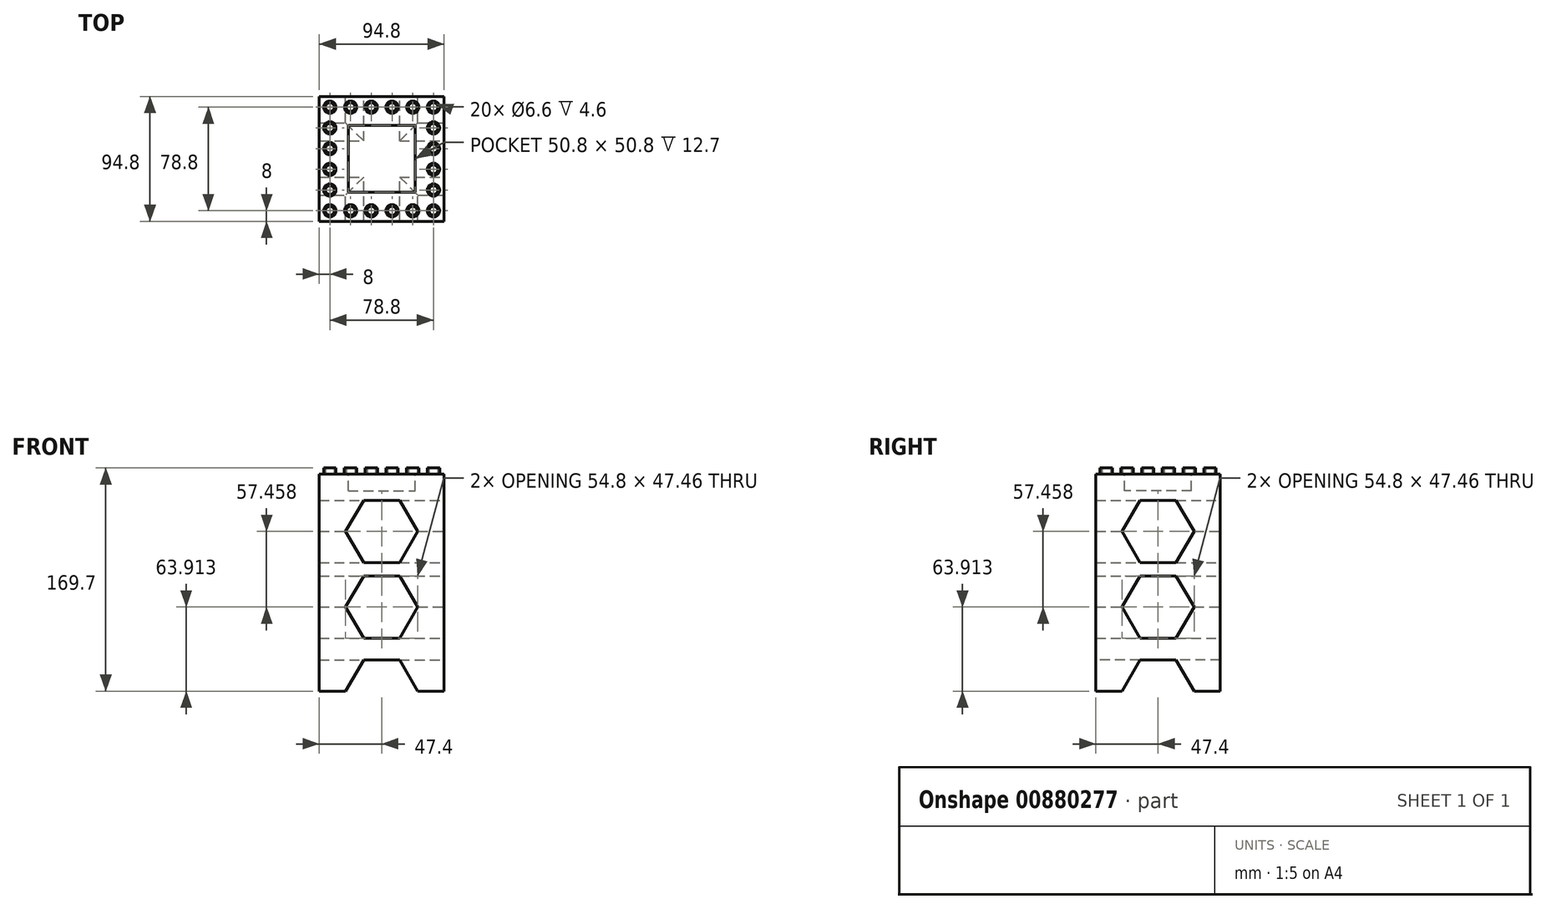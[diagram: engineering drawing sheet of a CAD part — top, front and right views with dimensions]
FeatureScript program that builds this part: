
annotation { "Feature Type Name" : "Feature", "Feature Type Description" : "" }
export const myFeature = defineFeature(function(context is Context, id is Id, definition is map)
    precondition{}
    {
        {
            var Q0;
            Q0=qCreatedBy(makeId("Top.planeOp"),FACE);
            var sketch = newSketch(context, id + "F0", { "sketchPlane" : qUnion([Q0])});
            skLineSegment(sketch, "E0.bottom", {"start": v(-25.4, 25.4) * mm, "end": v(25.4, 25.4) * mm});
            skLineSegment(sketch, "E0.top", {"start": v(-25.4, -25.4) * mm, "end": v(25.4, -25.4) * mm});
            skLineSegment(sketch, "E0.left", {"start": v(-25.4, 25.4) * mm, "end": v(-25.4, -25.4) * mm});
            skLineSegment(sketch, "E0.right", {"start": v(25.4, 25.4) * mm, "end": v(25.4, -25.4) * mm});
            skLineSegment(sketch, "E1.bottom", {"start": v(-47.4, 47.4) * mm, "end": v(47.4, 47.4) * mm});
            skLineSegment(sketch, "E1.top", {"start": v(-47.4, -47.4) * mm, "end": v(47.4, -47.4) * mm});
            skLineSegment(sketch, "E1.left", {"start": v(-47.4, 47.4) * mm, "end": v(-47.4, -47.4) * mm});
            skLineSegment(sketch, "E1.right", {"start": v(47.4, 47.4) * mm, "end": v(47.4, -47.4) * mm});
            skLineSegment(sketch, "E2", {"start": v(0, 25.4) * mm, "end": v(0, -25.4) * mm, "construction": true});
            skSolve(sketch);
        }
        {
            var Q0;
            Q0=makeQuery(id+"F0.imprint","IMPRINT",FACE,{"disambiguationData":[TD([[makeQuery(id+"F0.imprint","IMPRINT",EDGE,{"derivedFrom":sQuery(id+"F0.wireOp",EDGE,"E0.bottom")}),1.0]])]});
            var Q1;
            Q1=makeQuery(id+"F0.imprint","IMPRINT",FACE,{"disambiguationData":[TD([[makeQuery(id+"F0.imprint","IMPRINT",EDGE,{"derivedFrom":sQuery(id+"F0.wireOp",EDGE,"E0.bottom")}),-1.0]])]});
            extrude(context, id + "F1", {"entities" : qUnion([Q0, Q1]), "oppositeDirection" : true, "depth" : 165.1 * mm, "offsetDistance" : 25 * mm});
        }
        {
            var Q0;
            Q0=makeQuery(id+"F0.imprint","IMPRINT",FACE,{"disambiguationData":[TD([[makeQuery(id+"F0.imprint","IMPRINT",EDGE,{"derivedFrom":sQuery(id+"F0.wireOp",EDGE,"E0.bottom")}),-1.0]])]});
            extrude(context, id + "F2", {"entities" : qUnion([Q0]), "operationType" : NewBodyOperationType.REMOVE, "flatOperationType" : FlatOperationType.REMOVE, "oppositeDirection" : true, "depth" : 12.7 * mm, "offsetDistance" : 25 * mm, "domain" : OperationDomain.MODEL});
        }
        {
            var Q0;
            Q0=makeQuery(id+"F1.opExtrude","SWEPT_FACE",FACE,{"disambiguationData":[OSD([sQuery(id+"F0.wireOp",EDGE,"E1.right")])]});
            var sketch = newSketch(context, id + "F3", { "sketchPlane" : qUnion([Q0])});
            skLineSegment(sketch, "E3", {"start": v(0, -165.1) * mm, "end": v(0, -127.29) * mm});
            skCircle(sketch, "E4.cCircle", {"center": v(0, -165.1) * mm, "radius": 23.73 * mm, "construction": true});
            skLineSegment(sketch, "E4.0", {"start": v(-13.7, -141.37) * mm, "end": v(13.7, -141.37) * mm});
            skLineSegment(sketch, "E4.1", {"start": v(13.7, -141.37) * mm, "end": v(27.4, -165.1) * mm});
            skLineSegment(sketch, "E4.2", {"start": v(27.4, -165.1) * mm, "end": v(13.7, -188.83) * mm});
            skLineSegment(sketch, "E4.3", {"start": v(13.7, -188.83) * mm, "end": v(-13.7, -188.83) * mm});
            skLineSegment(sketch, "E4.4", {"start": v(-13.7, -188.83) * mm, "end": v(-27.4, -165.1) * mm});
            skLineSegment(sketch, "E4.5", {"start": v(-27.4, -165.1) * mm, "end": v(-13.7, -141.37) * mm});
            skPoint(sketch, "E4.0.midPoint", {"position": v(0, -141.37) * mm});
            skSolve(sketch);
        }
        {
            var Q0;
            Q0 = qSketchRegion(id + "F3", true);
            extrude(context, id + "F4", {"entities" : qUnion([Q0]), "operationType" : NewBodyOperationType.REMOVE, "oppositeDirection" : true, "depth" : 101.3 * mm, "offsetDistance" : 25 * mm});
        }
        {
            var Q0;
            Q0=makeQuery(id+"F1.opExtrude","SWEPT_FACE",FACE,{"disambiguationData":[OSD([sQuery(id+"F0.wireOp",EDGE,"E1.top")])]});
            var sketch = newSketch(context, id + "F5", { "sketchPlane" : qUnion([Q0])});
            skCircle(sketch, "E5.cCircle", {"center": v(0, -165.1) * mm, "radius": 23.73 * mm, "construction": true});
            skLineSegment(sketch, "E5.0", {"start": v(-13.7, -141.37) * mm, "end": v(13.7, -141.37) * mm});
            skLineSegment(sketch, "E5.1", {"start": v(13.7, -141.37) * mm, "end": v(27.4, -165.1) * mm});
            skLineSegment(sketch, "E5.2", {"start": v(27.4, -165.1) * mm, "end": v(13.7, -188.83) * mm});
            skLineSegment(sketch, "E5.3", {"start": v(13.7, -188.83) * mm, "end": v(-13.7, -188.83) * mm});
            skLineSegment(sketch, "E5.4", {"start": v(-13.7, -188.83) * mm, "end": v(-27.4, -165.1) * mm});
            skLineSegment(sketch, "E5.5", {"start": v(-27.4, -165.1) * mm, "end": v(-13.7, -141.37) * mm});
            skPoint(sketch, "E5.0.midPoint", {"position": v(0, -141.37) * mm});
            skSolve(sketch);
        }
        {
            var Q0;
            Q0=makeQuery(id+"F5.imprint","IMPRINT",FACE,{"disambiguationData":[TD([[makeQuery(id+"F5.imprint","IMPRINT",EDGE,{"derivedFrom":sQuery(id+"F5.wireOp",EDGE,"E5.0")}),-1.0]])]});
            extrude(context, id + "F6", {"entities" : qUnion([Q0]), "operationType" : NewBodyOperationType.REMOVE, "oppositeDirection" : true, "depth" : 114 * mm, "offsetDistance" : 25 * mm});
        }
        {
            var Q0;
            Q0=makeQuery(id+"F1.opExtrude","SWEPT_FACE",FACE,{"disambiguationData":[OSD([sQuery(id+"F0.wireOp",EDGE,"E1.bottom")])]});
            var sketch = newSketch(context, id + "F7", { "sketchPlane" : qUnion([Q0])});
            skCircle(sketch, "E6.cCircle", {"center": v(0, -43.73) * mm, "radius": 23.73 * mm, "construction": true});
            skLineSegment(sketch, "E6.0", {"start": v(-13.7, -20) * mm, "end": v(13.7, -20) * mm});
            skLineSegment(sketch, "E6.1", {"start": v(13.7, -20) * mm, "end": v(27.4, -43.73) * mm});
            skLineSegment(sketch, "E6.2", {"start": v(27.4, -43.73) * mm, "end": v(13.7, -67.46) * mm});
            skLineSegment(sketch, "E6.3", {"start": v(13.7, -67.46) * mm, "end": v(-13.7, -67.46) * mm});
            skLineSegment(sketch, "E6.4", {"start": v(-13.7, -67.46) * mm, "end": v(-27.4, -43.73) * mm});
            skLineSegment(sketch, "E6.5", {"start": v(-27.4, -43.73) * mm, "end": v(-13.7, -20) * mm});
            skPoint(sketch, "E6.0.midPoint", {"position": v(0, -20) * mm});
            skCircle(sketch, "E7.cCircle", {"center": v(0, -101.19) * mm, "radius": 23.73 * mm, "construction": true});
            skLineSegment(sketch, "E7.0", {"start": v(-13.7, -77.46) * mm, "end": v(13.7, -77.46) * mm});
            skLineSegment(sketch, "E7.1", {"start": v(13.7, -77.46) * mm, "end": v(27.4, -101.19) * mm});
            skLineSegment(sketch, "E7.2", {"start": v(27.4, -101.19) * mm, "end": v(13.7, -124.92) * mm});
            skLineSegment(sketch, "E7.3", {"start": v(13.7, -124.92) * mm, "end": v(-13.7, -124.92) * mm});
            skLineSegment(sketch, "E7.4", {"start": v(-13.7, -124.92) * mm, "end": v(-27.4, -101.19) * mm});
            skLineSegment(sketch, "E7.5", {"start": v(-27.4, -101.19) * mm, "end": v(-13.7, -77.46) * mm});
            skPoint(sketch, "E7.0.midPoint", {"position": v(0, -77.46) * mm});
            skLineSegment(sketch, "E8", {"start": v(60.92, 0) * mm, "end": v(60.92, -12.7) * mm});
            skSolve(sketch);
        }
        {
            var Q0;
            Q0=makeQuery(id+"F7.imprint","IMPRINT",FACE,{"disambiguationData":[TD([[makeQuery(id+"F7.imprint","IMPRINT",EDGE,{"derivedFrom":sQuery(id+"F7.wireOp",EDGE,"E6.0")}),-1.0]])]});
            extrude(context, id + "F8", {"entities" : qUnion([Q0]), "operationType" : NewBodyOperationType.REMOVE, "oppositeDirection" : true, "depth" : 110 * mm, "offsetDistance" : 25 * mm});
        }
        {
            var Q0;
            Q0=makeQuery(id+"F7.imprint","IMPRINT",FACE,{"disambiguationData":[TD([[makeQuery(id+"F7.imprint","IMPRINT",EDGE,{"derivedFrom":sQuery(id+"F7.wireOp",EDGE,"E7.0")}),-1.0]])]});
            extrude(context, id + "F9", {"entities" : qUnion([Q0]), "operationType" : NewBodyOperationType.REMOVE, "oppositeDirection" : true, "depth" : 114 * mm, "offsetDistance" : 25 * mm});
        }
        {
            var Q0;
            Q0=makeQuery(id+"F1.opExtrude","SWEPT_FACE",FACE,{"disambiguationData":[OSD([sQuery(id+"F0.wireOp",EDGE,"E1.right")])]});
            var sketch = newSketch(context, id + "F10", { "sketchPlane" : qUnion([Q0])});
            skCircle(sketch, "E9.cCircle", {"center": v(0, -43.73) * mm, "radius": 23.73 * mm, "construction": true});
            skLineSegment(sketch, "E9.0", {"start": v(-13.7, -20) * mm, "end": v(13.7, -20) * mm});
            skLineSegment(sketch, "E9.1", {"start": v(13.7, -20) * mm, "end": v(27.4, -43.73) * mm});
            skLineSegment(sketch, "E9.2", {"start": v(27.4, -43.73) * mm, "end": v(13.7, -67.46) * mm});
            skLineSegment(sketch, "E9.3", {"start": v(13.7, -67.46) * mm, "end": v(-13.7, -67.46) * mm});
            skLineSegment(sketch, "E9.4", {"start": v(-13.7, -67.46) * mm, "end": v(-27.4, -43.73) * mm});
            skLineSegment(sketch, "E9.5", {"start": v(-27.4, -43.73) * mm, "end": v(-13.7, -20) * mm});
            skPoint(sketch, "E9.0.midPoint", {"position": v(0, -20) * mm});
            skCircle(sketch, "E10.cCircle", {"center": v(0, -101.19) * mm, "radius": 23.73 * mm, "construction": true});
            skLineSegment(sketch, "E10.0", {"start": v(-13.7, -77.46) * mm, "end": v(13.7, -77.46) * mm});
            skLineSegment(sketch, "E10.1", {"start": v(13.7, -77.46) * mm, "end": v(27.4, -101.19) * mm});
            skLineSegment(sketch, "E10.2", {"start": v(27.4, -101.19) * mm, "end": v(13.7, -124.92) * mm});
            skLineSegment(sketch, "E10.3", {"start": v(13.7, -124.92) * mm, "end": v(-13.7, -124.92) * mm});
            skLineSegment(sketch, "E10.4", {"start": v(-13.7, -124.92) * mm, "end": v(-27.4, -101.19) * mm});
            skLineSegment(sketch, "E10.5", {"start": v(-27.4, -101.19) * mm, "end": v(-13.7, -77.46) * mm});
            skPoint(sketch, "E10.0.midPoint", {"position": v(0, -77.46) * mm});
            skSolve(sketch);
        }
        {
            var Q0;
            Q0=makeQuery(id+"F10.imprint","IMPRINT",FACE,{"disambiguationData":[TD([[makeQuery(id+"F10.imprint","IMPRINT",EDGE,{"derivedFrom":sQuery(id+"F10.wireOp",EDGE,"E9.0")}),-1.0]])]});
            var Q1;
            Q1=makeQuery(id+"F10.imprint","IMPRINT",FACE,{"disambiguationData":[TD([[makeQuery(id+"F10.imprint","IMPRINT",EDGE,{"derivedFrom":sQuery(id+"F10.wireOp",EDGE,"E10.0")}),-1.0]])]});
            extrude(context, id + "F11", {"entities" : qUnion([Q0, Q1]), "operationType" : NewBodyOperationType.REMOVE, "oppositeDirection" : true, "depth" : 115 * mm, "offsetDistance" : 25 * mm});
        }
        {
            var Q0;
            Q0=makeQuery(id+"F0.imprint","IMPRINT",FACE,{"disambiguationData":[TD([[makeQuery(id+"F0.imprint","IMPRINT",EDGE,{"derivedFrom":sQuery(id+"F0.wireOp",EDGE,"E0.bottom")}),1.0]])]});
            var sketch = newSketch(context, id + "F12", { "sketchPlane" : qUnion([Q0])});
            skCircle(sketch, "E11", {"center": v(39.4, 39.4) * mm, "radius": 4.7 * mm});
            skCircle(sketch, "E12.0.1.0", {"center": v(39.4, 23.64) * mm, "radius": 4.7 * mm});
            skCircle(sketch, "E12.0.2.0", {"center": v(39.4, 7.88) * mm, "radius": 4.7 * mm});
            skCircle(sketch, "E12.0.3.0", {"center": v(39.4, -7.88) * mm, "radius": 4.7 * mm});
            skCircle(sketch, "E12.0.4.0", {"center": v(39.4, -23.64) * mm, "radius": 4.7 * mm});
            skCircle(sketch, "E12.0.5.0", {"center": v(39.4, -39.4) * mm, "radius": 4.7 * mm});
            skCircle(sketch, "E12.1.0.0", {"center": v(23.64, 39.4) * mm, "radius": 4.7 * mm});
            skCircle(sketch, "E12.1.5.0", {"center": v(23.64, -39.4) * mm, "radius": 4.7 * mm});
            skCircle(sketch, "E12.2.0.0", {"center": v(7.88, 39.4) * mm, "radius": 4.7 * mm});
            skCircle(sketch, "E12.2.5.0", {"center": v(7.88, -39.4) * mm, "radius": 4.7 * mm});
            skCircle(sketch, "E12.3.0.0", {"center": v(-7.88, 39.4) * mm, "radius": 4.7 * mm});
            skCircle(sketch, "E12.3.5.0", {"center": v(-7.88, -39.4) * mm, "radius": 4.7 * mm});
            skCircle(sketch, "E12.4.0.0", {"center": v(-23.64, 39.4) * mm, "radius": 4.7 * mm});
            skCircle(sketch, "E12.4.5.0", {"center": v(-23.64, -39.4) * mm, "radius": 4.7 * mm});
            skCircle(sketch, "E12.5.0.0", {"center": v(-39.4, 39.4) * mm, "radius": 4.7 * mm});
            skCircle(sketch, "E12.5.1.0", {"center": v(-39.4, 23.64) * mm, "radius": 4.7 * mm});
            skCircle(sketch, "E12.5.2.0", {"center": v(-39.4, 7.88) * mm, "radius": 4.7 * mm});
            skCircle(sketch, "E12.5.3.0", {"center": v(-39.4, -7.88) * mm, "radius": 4.7 * mm});
            skCircle(sketch, "E12.5.4.0", {"center": v(-39.4, -23.64) * mm, "radius": 4.7 * mm});
            skCircle(sketch, "E12.5.5.0", {"center": v(-39.4, -39.4) * mm, "radius": 4.7 * mm});
            skLineSegment(sketch, "E12.direction1", {"start": v(39.4, 39.4) * mm, "end": v(23.64, 39.4) * mm, "construction": true});
            skLineSegment(sketch, "E12.direction2", {"start": v(39.4, 39.4) * mm, "end": v(39.4, 23.64) * mm, "construction": true});
            skCircle(sketch, "E13", {"center": v(39.4, 39.4) * mm, "radius": 3.3 * mm});
            skCircle(sketch, "E14.0.1.0", {"center": v(39.4, 23.64) * mm, "radius": 3.3 * mm});
            skCircle(sketch, "E14.0.2.0", {"center": v(39.4, 7.88) * mm, "radius": 3.3 * mm});
            skCircle(sketch, "E14.0.3.0", {"center": v(39.4, -7.88) * mm, "radius": 3.3 * mm});
            skCircle(sketch, "E14.0.4.0", {"center": v(39.4, -23.64) * mm, "radius": 3.3 * mm});
            skCircle(sketch, "E14.0.5.0", {"center": v(39.4, -39.4) * mm, "radius": 3.3 * mm});
            skCircle(sketch, "E14.1.0.0", {"center": v(23.64, 39.4) * mm, "radius": 3.3 * mm});
            skCircle(sketch, "E14.1.5.0", {"center": v(23.64, -39.4) * mm, "radius": 3.3 * mm});
            skCircle(sketch, "E14.2.0.0", {"center": v(7.88, 39.4) * mm, "radius": 3.3 * mm});
            skCircle(sketch, "E14.2.5.0", {"center": v(7.88, -39.4) * mm, "radius": 3.3 * mm});
            skCircle(sketch, "E14.3.0.0", {"center": v(-7.88, 39.4) * mm, "radius": 3.3 * mm});
            skCircle(sketch, "E14.3.5.0", {"center": v(-7.88, -39.4) * mm, "radius": 3.3 * mm});
            skCircle(sketch, "E14.4.0.0", {"center": v(-23.64, 39.4) * mm, "radius": 3.3 * mm});
            skCircle(sketch, "E14.4.5.0", {"center": v(-23.64, -39.4) * mm, "radius": 3.3 * mm});
            skCircle(sketch, "E14.5.0.0", {"center": v(-39.4, 39.4) * mm, "radius": 3.3 * mm});
            skCircle(sketch, "E14.5.1.0", {"center": v(-39.4, 23.64) * mm, "radius": 3.3 * mm});
            skCircle(sketch, "E14.5.2.0", {"center": v(-39.4, 7.88) * mm, "radius": 3.3 * mm});
            skCircle(sketch, "E14.5.3.0", {"center": v(-39.4, -7.88) * mm, "radius": 3.3 * mm});
            skCircle(sketch, "E14.5.4.0", {"center": v(-39.4, -23.64) * mm, "radius": 3.3 * mm});
            skCircle(sketch, "E14.5.5.0", {"center": v(-39.4, -39.4) * mm, "radius": 3.3 * mm});
            skSolve(sketch);
        }
        {
            var Q0;
            Q0=makeQuery(id+"F12.imprint","IMPRINT",FACE,{"disambiguationData":[TD([[makeQuery(id+"F12.imprint","IMPRINT",EDGE,{"derivedFrom":sQuery(id+"F12.wireOp",EDGE,"E12.5.0.0")}),1.0]])]});
            var Q1;
            Q1=makeQuery(id+"F12.imprint","IMPRINT",FACE,{"disambiguationData":[TD([[makeQuery(id+"F12.imprint","IMPRINT",EDGE,{"derivedFrom":sQuery(id+"F12.wireOp",EDGE,"E12.5.1.0")}),1.0]])]});
            var Q2;
            Q2=makeQuery(id+"F12.imprint","IMPRINT",FACE,{"disambiguationData":[TD([[makeQuery(id+"F12.imprint","IMPRINT",EDGE,{"derivedFrom":sQuery(id+"F12.wireOp",EDGE,"E12.5.2.0")}),1.0]])]});
            var Q3;
            Q3=makeQuery(id+"F12.imprint","IMPRINT",FACE,{"disambiguationData":[TD([[makeQuery(id+"F12.imprint","IMPRINT",EDGE,{"derivedFrom":sQuery(id+"F12.wireOp",EDGE,"E12.5.3.0")}),1.0]])]});
            var Q4;
            Q4=makeQuery(id+"F12.imprint","IMPRINT",FACE,{"disambiguationData":[TD([[makeQuery(id+"F12.imprint","IMPRINT",EDGE,{"derivedFrom":sQuery(id+"F12.wireOp",EDGE,"E12.5.4.0")}),1.0]])]});
            var Q5;
            Q5=makeQuery(id+"F12.imprint","IMPRINT",FACE,{"disambiguationData":[TD([[makeQuery(id+"F12.imprint","IMPRINT",EDGE,{"derivedFrom":sQuery(id+"F12.wireOp",EDGE,"E12.5.5.0")}),1.0]])]});
            var Q6;
            Q6=makeQuery(id+"F12.imprint","IMPRINT",FACE,{"disambiguationData":[TD([[makeQuery(id+"F12.imprint","IMPRINT",EDGE,{"derivedFrom":sQuery(id+"F12.wireOp",EDGE,"E12.4.5.0")}),1.0]])]});
            var Q7;
            Q7=makeQuery(id+"F12.imprint","IMPRINT",FACE,{"disambiguationData":[TD([[makeQuery(id+"F12.imprint","IMPRINT",EDGE,{"derivedFrom":sQuery(id+"F12.wireOp",EDGE,"E12.3.5.0")}),1.0]])]});
            var Q8;
            Q8=makeQuery(id+"F12.imprint","IMPRINT",FACE,{"disambiguationData":[TD([[makeQuery(id+"F12.imprint","IMPRINT",EDGE,{"derivedFrom":sQuery(id+"F12.wireOp",EDGE,"E12.4.0.0")}),1.0]])]});
            var Q9;
            Q9=makeQuery(id+"F12.imprint","IMPRINT",FACE,{"disambiguationData":[TD([[makeQuery(id+"F12.imprint","IMPRINT",EDGE,{"derivedFrom":sQuery(id+"F12.wireOp",EDGE,"E12.3.0.0")}),1.0]])]});
            var Q10;
            Q10=makeQuery(id+"F12.imprint","IMPRINT",FACE,{"disambiguationData":[TD([[makeQuery(id+"F12.imprint","IMPRINT",EDGE,{"derivedFrom":sQuery(id+"F12.wireOp",EDGE,"E12.2.0.0")}),1.0]])]});
            var Q11;
            Q11=makeQuery(id+"F12.imprint","IMPRINT",FACE,{"disambiguationData":[TD([[makeQuery(id+"F12.imprint","IMPRINT",EDGE,{"derivedFrom":sQuery(id+"F12.wireOp",EDGE,"E12.1.0.0")}),1.0]])]});
            var Q12;
            Q12=makeQuery(id+"F12.imprint","IMPRINT",FACE,{"disambiguationData":[TD([[makeQuery(id+"F12.imprint","IMPRINT",EDGE,{"derivedFrom":sQuery(id+"F12.wireOp",EDGE,"E11")}),1.0]])]});
            var Q13;
            Q13=makeQuery(id+"F12.imprint","IMPRINT",FACE,{"disambiguationData":[TD([[makeQuery(id+"F12.imprint","IMPRINT",EDGE,{"derivedFrom":sQuery(id+"F12.wireOp",EDGE,"E12.0.1.0")}),1.0]])]});
            var Q14;
            Q14=makeQuery(id+"F12.imprint","IMPRINT",FACE,{"disambiguationData":[TD([[makeQuery(id+"F12.imprint","IMPRINT",EDGE,{"derivedFrom":sQuery(id+"F12.wireOp",EDGE,"E12.0.2.0")}),1.0]])]});
            var Q15;
            Q15=makeQuery(id+"F12.imprint","IMPRINT",FACE,{"disambiguationData":[TD([[makeQuery(id+"F12.imprint","IMPRINT",EDGE,{"derivedFrom":sQuery(id+"F12.wireOp",EDGE,"E12.0.3.0")}),1.0]])]});
            var Q16;
            Q16=makeQuery(id+"F12.imprint","IMPRINT",FACE,{"disambiguationData":[TD([[makeQuery(id+"F12.imprint","IMPRINT",EDGE,{"derivedFrom":sQuery(id+"F12.wireOp",EDGE,"E12.0.4.0")}),1.0]])]});
            var Q17;
            Q17=makeQuery(id+"F12.imprint","IMPRINT",FACE,{"disambiguationData":[TD([[makeQuery(id+"F12.imprint","IMPRINT",EDGE,{"derivedFrom":sQuery(id+"F12.wireOp",EDGE,"E12.0.5.0")}),1.0]])]});
            var Q18;
            Q18=makeQuery(id+"F12.imprint","IMPRINT",FACE,{"disambiguationData":[TD([[makeQuery(id+"F12.imprint","IMPRINT",EDGE,{"derivedFrom":sQuery(id+"F12.wireOp",EDGE,"E12.1.5.0")}),1.0]])]});
            var Q19;
            Q19=makeQuery(id+"F12.imprint","IMPRINT",FACE,{"disambiguationData":[TD([[makeQuery(id+"F12.imprint","IMPRINT",EDGE,{"derivedFrom":sQuery(id+"F12.wireOp",EDGE,"E12.2.5.0")}),1.0]])]});
            extrude(context, id + "F13", {"entities" : qUnion([Q0, Q1, Q2, Q3, Q4, Q5, Q6, Q7, Q8, Q9, Q10, Q11, Q12, Q13, Q14, Q15, Q16, Q17, Q18, Q19]), "operationType" : NewBodyOperationType.ADD, "depth" : 4.6 * mm, "offsetDistance" : 25 * mm});
        }
    });
